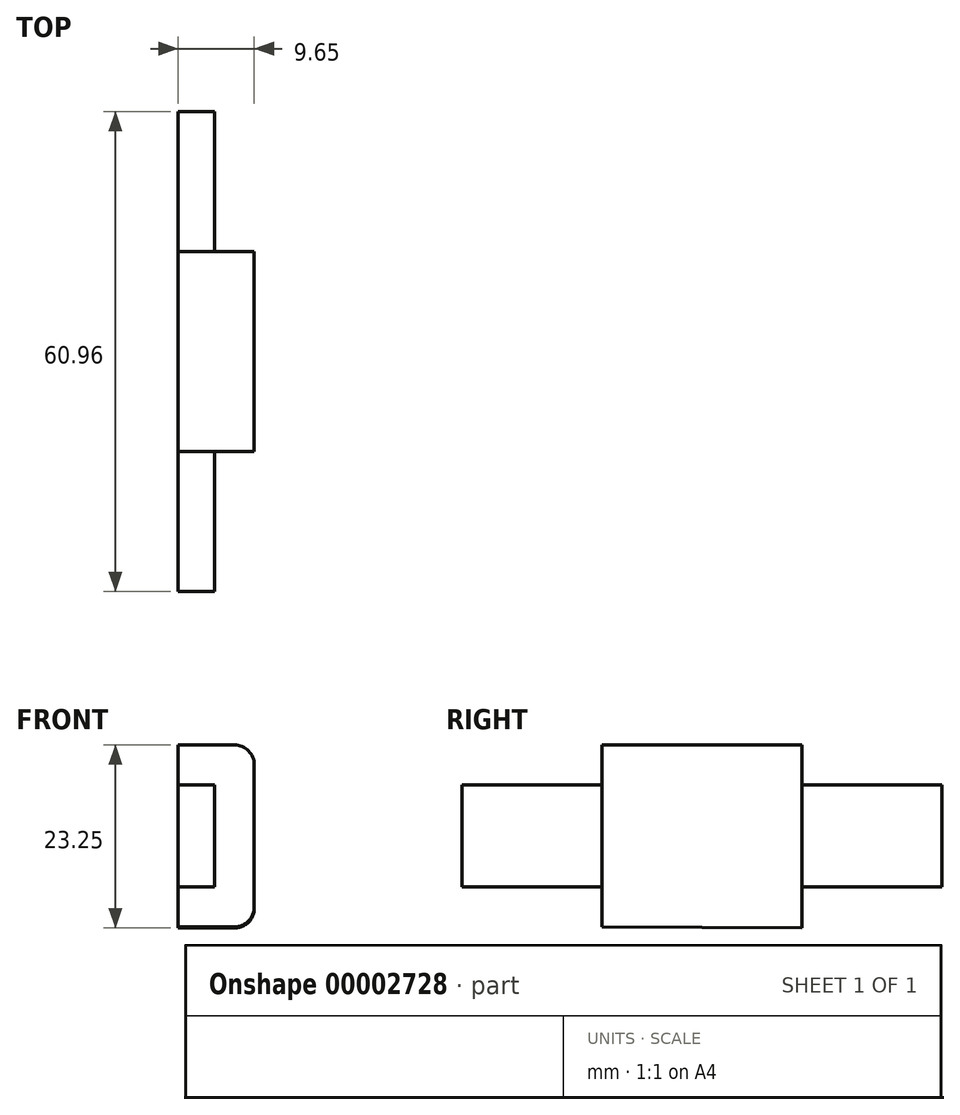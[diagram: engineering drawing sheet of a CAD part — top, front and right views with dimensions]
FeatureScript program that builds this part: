
annotation { "Feature Type Name" : "Feature", "Feature Type Description" : "" }
export const myFeature = defineFeature(function(context is Context, id is Id, definition is map)
    precondition{}
    {
        {
            var Q0;
            Q0=qCreatedBy(makeId("Front.planeOp"),FACE);
            var sketch = newSketch(context, id + "F0", { "sketchPlane" : qUnion([Q0])});
            skLineSegment(sketch, "E0.bottom", {"start": v(0, 0) * mm, "end": v(4.57, 0) * mm});
            skLineSegment(sketch, "E0.top", {"start": v(0, -12.95) * mm, "end": v(4.57, -12.95) * mm});
            skLineSegment(sketch, "E0.left", {"start": v(0, 0) * mm, "end": v(0, -12.95) * mm});
            skLineSegment(sketch, "E0.right", {"start": v(4.57, 0) * mm, "end": v(4.57, -12.95) * mm});
            skSolve(sketch);
        }
        {
            var Q0;
            Q0=makeQuery(id+"F0.imprint","IMPRINT",FACE,{"disambiguationData":[TD([[makeQuery(id+"F0.imprint","IMPRINT",EDGE,{"derivedFrom":sQuery(id+"F0.wireOp",EDGE,"E0.bottom")}),-1.0]])]});
            extrude(context, id + "F1", {"entities" : qUnion([Q0]), "depth" : 60.96 * mm});
        }
        {
            var Q0;
            Q0=makeQuery(id+"F1.opExtrude","SWEPT_FACE",FACE,{"disambiguationData":[OSD([sQuery(id+"F0.wireOp",EDGE,"E0.left")])]});
            var sketch = newSketch(context, id + "F2", { "sketchPlane" : qUnion([Q0])});
            skLineSegment(sketch, "E1", {"start": v(30.48, -12.95) * mm, "end": v(30.48, -18.03) * mm, "construction": true});
            skLineSegment(sketch, "E2", {"start": v(30.48, -18.03) * mm, "end": v(43.18, -18.03) * mm, "construction": true});
            skLineSegment(sketch, "E3", {"start": v(43.18, -18.03) * mm, "end": v(43.18, 5.08) * mm, "construction": true});
            skLineSegment(sketch, "E4", {"start": v(43.18, 5.08) * mm, "end": v(17.78, 5.08) * mm, "construction": true});
            skLineSegment(sketch, "E5", {"start": v(17.78, 5.08) * mm, "end": v(17.78, -18.17) * mm, "construction": true});
            skLineSegment(sketch, "E6", {"start": v(17.78, -18.17) * mm, "end": v(30.48, -18.03) * mm, "construction": true});
            skSolve(sketch);
        }
        {
            var Q0;
            Q0=makeQuery(id+"F1.opExtrude","SWEPT_FACE",FACE,{"disambiguationData":[OSD([sQuery(id+"F0.wireOp",EDGE,"E0.left")])]});
            var sketch = newSketch(context, id + "F3", { "sketchPlane" : qUnion([Q0])});
            skLineSegment(sketch, "E7", {"start": v(43.18, -18.03) * mm, "end": v(43.18, 5.08) * mm});
            skLineSegment(sketch, "E8", {"start": v(43.18, 5.08) * mm, "end": v(17.78, 5.08) * mm});
            skLineSegment(sketch, "E9", {"start": v(17.78, 5.08) * mm, "end": v(17.78, -18.17) * mm});
            skLineSegment(sketch, "E10", {"start": v(17.78, -18.17) * mm, "end": v(43.18, -18.03) * mm});
            skSolve(sketch);
        }
        {
            var Q0;
            {var subQ0=sQuery(id+"F0.wireOp",EDGE,"E0.left");var subQ1=makeQuery(id+"F1.opExtrude","SWEPT_EDGE",EDGE,{"disambiguationData":[OSD([sQuery(id+"F0.wireOp",EDGE,"E0.top"),subQ0])]});var subQ4=sQuery(id+"F3.wireOp",EDGE,"E7");var subQ5=makeQuery(id+"F3.imprint","INTERSECT",VERTEX,{"derivedFrom":[subQ1,subQ4]});var subQ7=sQuery(id+"F3.wireOp",EDGE,"E10");var subQ12=sQuery(id+"F3.wireOp",EDGE,"E8");Q0=qUnion([makeQuery(id+"F3.imprint","IMPRINT",FACE,{"disambiguationData":[TD([[makeQuery(id+"F3.imprint","IMPRINT",EDGE,{"derivedFrom":subQ7}),1.0]])]}),makeQuery(id+"F3.imprint","IMPRINT",FACE,{"disambiguationData":[TD([[makeQuery(id+"F3.imprint","IMPRINT",EDGE,{"derivedFrom":subQ12}),1.0]])]}),makeQuery(id+"F3.imprint","IMPRINT",FACE,{"disambiguationData":[TD([[makeQuery(id+"F3.imprint","IMPRINT",EDGE,{"disambiguationData":[TD([[subQ5,-1.0]])],"derivedFrom":subQ4}),1.0]])]})]);}
            extrude(context, id + "F4", {"entities" : qUnion([Q0]), "operationType" : NewBodyOperationType.ADD, "oppositeDirection" : true, "depth" : 9.65 * mm});
        }
        {
            var Q0;
            Q0=makeQuery(id+"F4.opExtrude","CAP_EDGE",EDGE,{"disambiguationData":[OSD([sQuery(id+"F3.wireOp",EDGE,"E10")])],"isStart":false});
            var Q1;
            Q1=makeQuery(id+"F4.opExtrude","CAP_EDGE",EDGE,{"disambiguationData":[OSD([sQuery(id+"F3.wireOp",EDGE,"E8")])],"isStart":false});
            fillet(context, id + "F5", {"entities" : qUnion([Q0, Q1]), "radius" : 2.54 * mm, "tangentPropagation" : true, "allowEdgeOverflow" : false});
        }
    });
